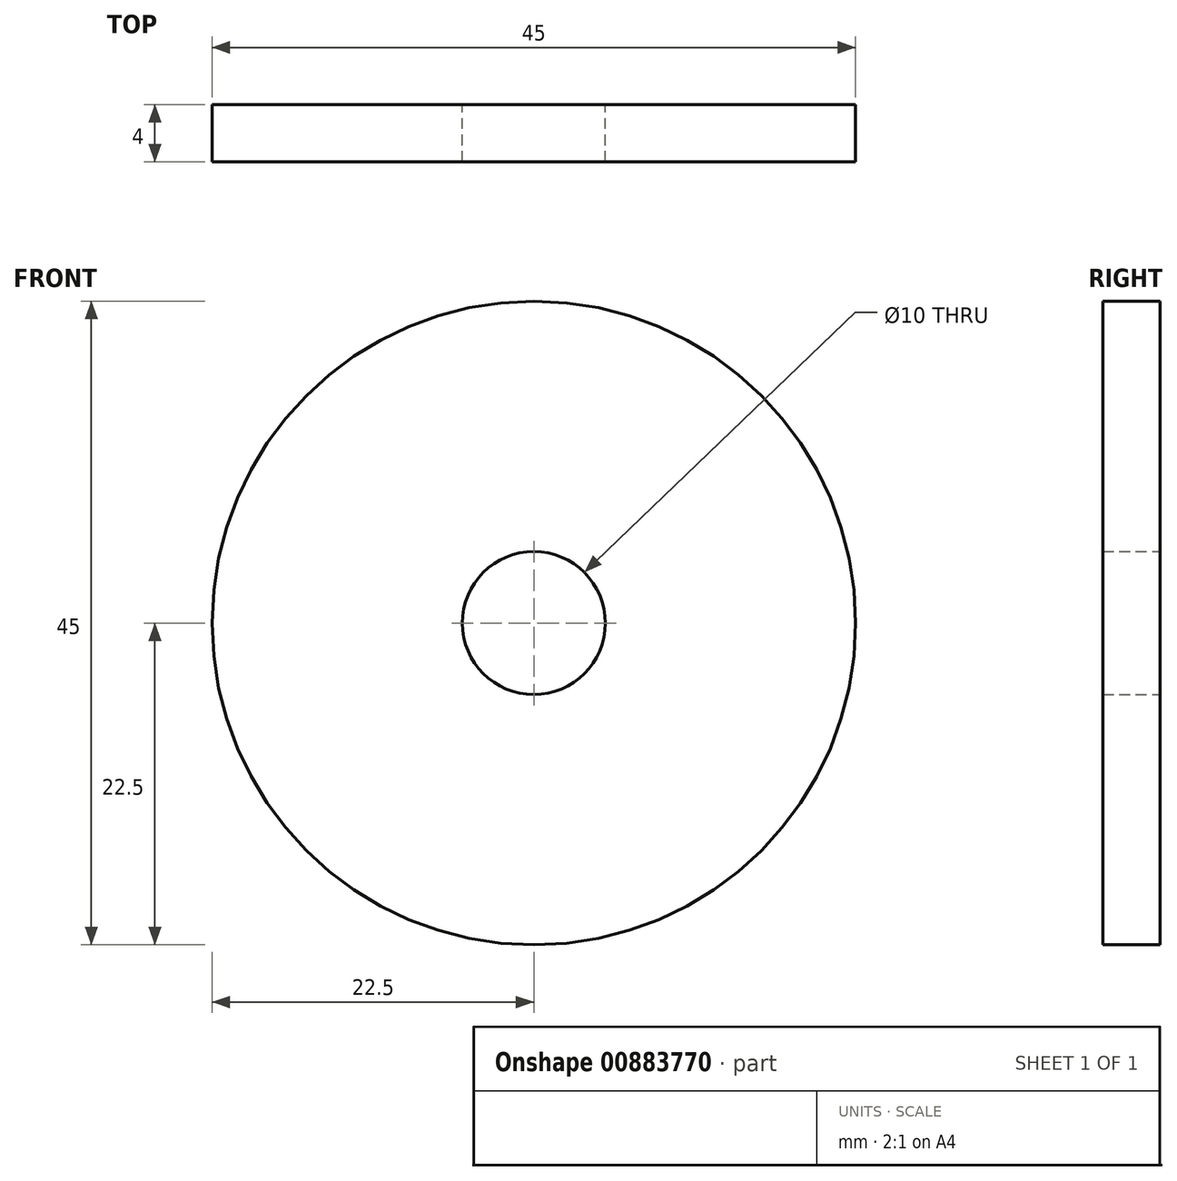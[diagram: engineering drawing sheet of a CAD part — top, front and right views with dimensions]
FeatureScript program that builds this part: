
annotation { "Feature Type Name" : "Feature", "Feature Type Description" : "" }
export const myFeature = defineFeature(function(context is Context, id is Id, definition is map)
    precondition{}
    {
        {
            var Q0;
            Q0=qCreatedBy(makeId("Front.planeOp"),FACE);
            var sketch = newSketch(context, id + "F0", { "sketchPlane" : qUnion([Q0])});
            skCircle(sketch, "E0", {"center": v(0, 0) * mm, "radius": 22.5 * mm});
            skCircle(sketch, "E1", {"center": v(0, 0) * mm, "radius": 5 * mm});
            skSolve(sketch);
        }
        {
            var Q0;
            Q0 = qSketchRegion(id + "F0", true);
            extrude(context, id + "F1", {"entities" : qUnion([Q0]), "depth" : 4 * mm, "offsetDistance" : 25 * mm});
        }
    });
